# Revit family: Deca_Coluna suspensa para lavatório_Monte Carlo.Vogue Plus_CS.1
name_source: partatom
category: Plumbing Fixtures
units: mm (PartAtom-declared; Revit-internal decimal feet)

## family parameters
Cut with Voids When Loaded = No
Host = Face
Part Type = Normal
Room Calculation Point = No
Round Connector Dimension = Use Diameter
Shared = No

## types (3) — shared parameters
Acompanha o Produto = -
Aprovado por = quattroD
Atendimento ao Cliente = 0800-0117073
Categoria = LAVATORIOS
Composição Anel Vedação = -
Composição Assento = -
Composição Básica = Argila, feldspato, caulim, vidrados e corantes inorgânicos.
Composição Componente = Não Possui
Consumo = -
Cor Interna = -
Cor Secundária = -
Cores Componente = Não Possui
Criado por = quattroD
Código Pai = CS.1
Description = Coluna suspensa para lavatório
Informações Complementares = -
Itens de Instalação = -
Linha = Coluna Univ. Médio
Manufacturer = Deca
Norma = NBR-16728-1;NBR-16728-2
Pressão máx. funcionamento = -
Pressão mín. Aquec. Acúmulo = -
Pressão mín. Aquec. Passagem = -
Pressão mín. funcionamento = -
Saída de Esgoto = -
Segmento = Banheiro Médio
Tipo de dispositivo economizador = -
Tipo de mecanismo utilizado = -
Tipo de rosca de entrada = -
Tipo de rosca de saída = -
URL = www.deca.com.br
Vazão na Pressão máx. (L/min) = -
Vazão na Pressão mín. (L/min) = -
zero-valued in all types: Default Elevation

## per-type parameters (varying)
| type | Cor Principal | Material | Model | Peso Líquido (Kg) |
| CS.1.37_Creme | Creme | Deca_Creme | CS.1.37 | 7.83 |
| CS.1.17_Branco | Branco | Deca_Branco | CS.1.17 | 7.83 |
| CS.1.95_Ébano | Ébano | Deca_Ébano | CS.1.95 | 7.835 |

## geometry (parser evidence)
native form markers: Sweep x2
no freeform markers — native parametric forms only
